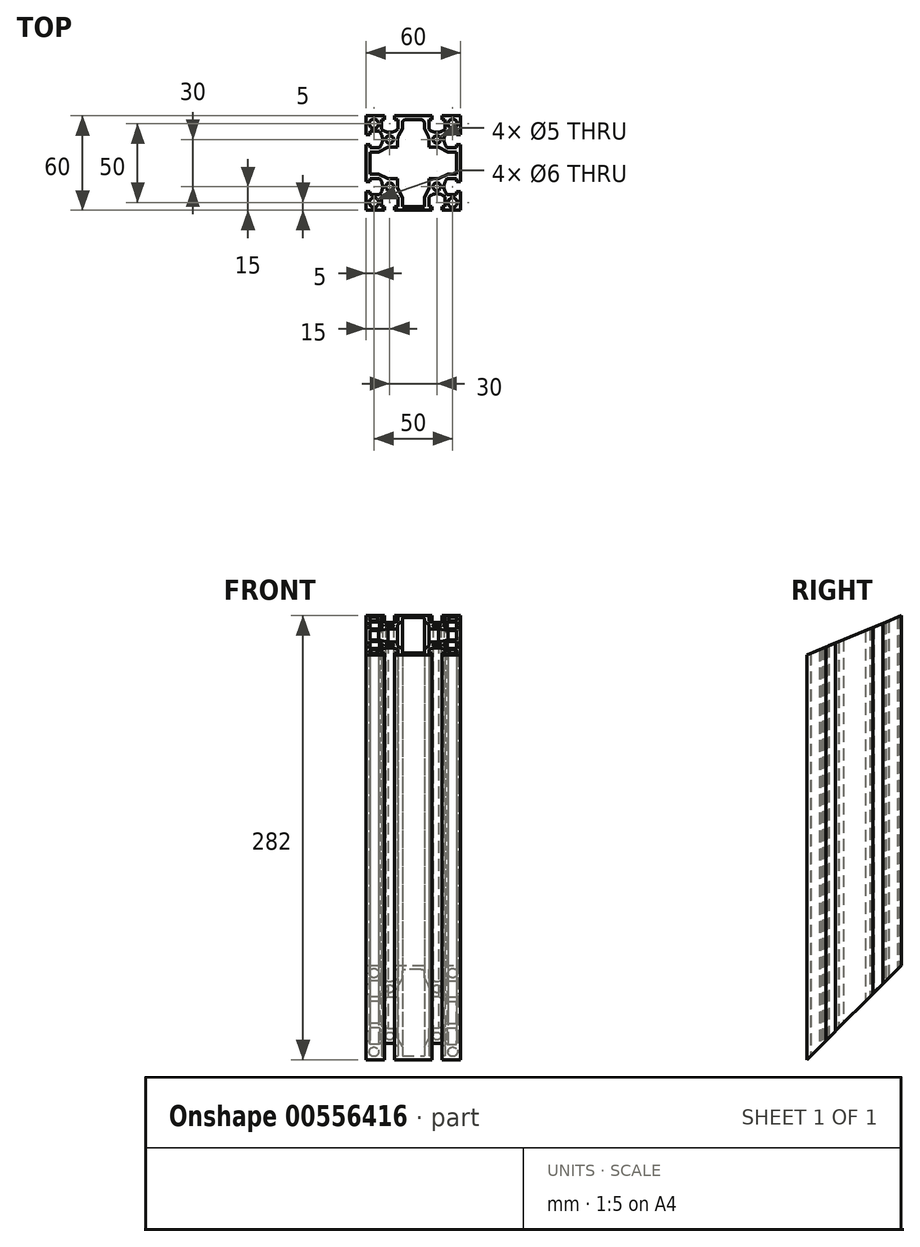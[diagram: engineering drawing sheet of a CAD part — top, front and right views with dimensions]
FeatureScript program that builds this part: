
annotation { "Feature Type Name" : "Feature", "Feature Type Description" : "" }
export const myFeature = defineFeature(function(context is Context, id is Id, definition is map)
    precondition{}
    {
        {
            var Q0;
            Q0=qCreatedBy(makeId("Top.planeOp"),FACE);
            var sketch = newSketch(context, id + "F0", { "sketchPlane" : qUnion([Q0])});
            skLineSegment(sketch, "E0.bottom", {"start": v(30, -30) * mm, "end": v(-30, -30) * mm});
            skLineSegment(sketch, "E0.top", {"start": v(30, 30) * mm, "end": v(-30, 30) * mm});
            skLineSegment(sketch, "E0.left", {"start": v(30, -30) * mm, "end": v(30, 30) * mm});
            skLineSegment(sketch, "E0.right", {"start": v(-30, -30) * mm, "end": v(-30, 30) * mm});
            skPoint(sketch, "E0.middle", {"position": v(0, 0) * mm});
            skLineSegment(sketch, "E1.top", {"start": v(-11.85, 30) * mm, "end": v(-18.15, 30) * mm});
            skLineSegment(sketch, "E1.left", {"start": v(-11.85, 27.5) * mm, "end": v(-11.85, 30) * mm});
            skLineSegment(sketch, "E1.right", {"start": v(-18.15, 27.5) * mm, "end": v(-18.15, 30) * mm});
            skPoint(sketch, "E1.middle", {"position": v(-15, 28.75) * mm});
            skLineSegment(sketch, "E2.bottom", {"start": v(-9.85, 27.5) * mm, "end": v(-11.85, 27.5) * mm});
            skLineSegment(sketch, "E2.left", {"start": v(-9.85, 27.5) * mm, "end": v(-9.85, 21.55) * mm});
            skLineSegment(sketch, "E2.right", {"start": v(-20.15, 27.5) * mm, "end": v(-20.15, 21.55) * mm});
            skPoint(sketch, "E2.middle", {"position": v(-15, 24.52) * mm});
            skArc(sketch, "E3", {"start": v(-20.15, 21.55) * mm, "mid": v(-15, 19.5) * mm, "end": v(-9.85, 21.55) * mm});
            skPoint(sketch, "E4.MirrorP", {"position": v(15, 24.52) * mm});
            skPoint(sketch, "E5.MirrorP", {"position": v(15, 28.75) * mm});
            skLineSegment(sketch, "E6.MirrorCS", {"start": v(11.85, 27.5) * mm, "end": v(11.85, 30) * mm});
            skLineSegment(sketch, "E7.MirrorCS", {"start": v(18.15, 27.5) * mm, "end": v(18.15, 30) * mm});
            skLineSegment(sketch, "E8.MirrorCS", {"start": v(9.85, 27.5) * mm, "end": v(11.85, 27.5) * mm});
            skLineSegment(sketch, "E9.MirrorCS", {"start": v(9.85, 27.5) * mm, "end": v(9.85, 21.55) * mm});
            skArc(sketch, "E10.MirrorCS", {"start": v(20.15, 21.55) * mm, "mid": v(15, 19.5) * mm, "end": v(9.85, 21.55) * mm});
            skLineSegment(sketch, "E11.MirrorCS", {"start": v(20.15, 27.5) * mm, "end": v(20.15, 21.55) * mm});
            skLineSegment(sketch, "E12.MirrorCS", {"start": v(11.85, 30) * mm, "end": v(18.15, 30) * mm});
            skLineSegment(sketch, "E13.1.0", {"start": v(27.5, 20.15) * mm, "end": v(21.55, 20.15) * mm});
            skLineSegment(sketch, "E13.1.1", {"start": v(27.5, 9.85) * mm, "end": v(21.55, 9.85) * mm});
            skArc(sketch, "E13.1.2", {"start": v(21.55, 20.15) * mm, "mid": v(19.5, 15) * mm, "end": v(21.55, 9.85) * mm});
            skLineSegment(sketch, "E13.1.3", {"start": v(27.5, -9.85) * mm, "end": v(21.55, -9.85) * mm});
            skLineSegment(sketch, "E13.1.4", {"start": v(27.5, -20.15) * mm, "end": v(21.55, -20.15) * mm});
            skPoint(sketch, "E13.1.5", {"position": v(28.75, 15) * mm});
            skPoint(sketch, "E13.1.6", {"position": v(28.75, -15) * mm});
            skArc(sketch, "E13.1.7", {"start": v(21.55, -20.15) * mm, "mid": v(19.5, -15) * mm, "end": v(21.55, -9.85) * mm});
            skPoint(sketch, "E13.1.8", {"position": v(24.52, -15) * mm});
            skPoint(sketch, "E13.1.9", {"position": v(24.52, 15) * mm});
            skLineSegment(sketch, "E13.1.10", {"start": v(27.5, 9.85) * mm, "end": v(27.5, 20.15) * mm});
            skLineSegment(sketch, "E13.1.11", {"start": v(27.5, -11.85) * mm, "end": v(27.5, -18.15) * mm});
            skLineSegment(sketch, "E13.1.12", {"start": v(30, 11.85) * mm, "end": v(30, 18.15) * mm});
            skLineSegment(sketch, "E13.1.13", {"start": v(30, -11.85) * mm, "end": v(30, -18.15) * mm});
            skLineSegment(sketch, "E13.1.14", {"start": v(27.5, 18.15) * mm, "end": v(30, 18.15) * mm});
            skLineSegment(sketch, "E13.1.15", {"start": v(27.5, 11.85) * mm, "end": v(30, 11.85) * mm});
            skLineSegment(sketch, "E13.1.16", {"start": v(27.5, 11.85) * mm, "end": v(27.5, 18.15) * mm});
            skLineSegment(sketch, "E13.1.17", {"start": v(27.5, -9.85) * mm, "end": v(27.5, -20.15) * mm});
            skLineSegment(sketch, "E13.1.18", {"start": v(27.5, -18.15) * mm, "end": v(30, -18.15) * mm});
            skLineSegment(sketch, "E13.1.19", {"start": v(27.5, -11.85) * mm, "end": v(30, -11.85) * mm});
            skLineSegment(sketch, "E13.2.0", {"start": v(20.15, -27.5) * mm, "end": v(20.15, -21.55) * mm});
            skLineSegment(sketch, "E13.2.1", {"start": v(9.85, -27.5) * mm, "end": v(9.85, -21.55) * mm});
            skArc(sketch, "E13.2.2", {"start": v(20.15, -21.55) * mm, "mid": v(15, -19.5) * mm, "end": v(9.85, -21.55) * mm});
            skLineSegment(sketch, "E13.2.3", {"start": v(-9.85, -27.5) * mm, "end": v(-9.85, -21.55) * mm});
            skLineSegment(sketch, "E13.2.4", {"start": v(-20.15, -27.5) * mm, "end": v(-20.15, -21.55) * mm});
            skPoint(sketch, "E13.2.5", {"position": v(15, -28.75) * mm});
            skPoint(sketch, "E13.2.6", {"position": v(-15, -28.75) * mm});
            skArc(sketch, "E13.2.7", {"start": v(-20.15, -21.55) * mm, "mid": v(-15, -19.5) * mm, "end": v(-9.85, -21.55) * mm});
            skPoint(sketch, "E13.2.8", {"position": v(-15, -24.52) * mm});
            skPoint(sketch, "E13.2.9", {"position": v(15, -24.52) * mm});
            skLineSegment(sketch, "E13.2.10", {"start": v(9.85, -27.5) * mm, "end": v(20.15, -27.5) * mm});
            skLineSegment(sketch, "E13.2.11", {"start": v(-11.85, -27.5) * mm, "end": v(-18.15, -27.5) * mm});
            skLineSegment(sketch, "E13.2.12", {"start": v(11.85, -30) * mm, "end": v(18.15, -30) * mm});
            skLineSegment(sketch, "E13.2.13", {"start": v(-11.85, -30) * mm, "end": v(-18.15, -30) * mm});
            skLineSegment(sketch, "E13.2.14", {"start": v(18.15, -27.5) * mm, "end": v(18.15, -30) * mm});
            skLineSegment(sketch, "E13.2.15", {"start": v(11.85, -27.5) * mm, "end": v(11.85, -30) * mm});
            skLineSegment(sketch, "E13.2.16", {"start": v(11.85, -27.5) * mm, "end": v(18.15, -27.5) * mm});
            skLineSegment(sketch, "E13.2.17", {"start": v(-9.85, -27.5) * mm, "end": v(-20.15, -27.5) * mm});
            skLineSegment(sketch, "E13.2.18", {"start": v(-18.15, -27.5) * mm, "end": v(-18.15, -30) * mm});
            skLineSegment(sketch, "E13.2.19", {"start": v(-11.85, -27.5) * mm, "end": v(-11.85, -30) * mm});
            skLineSegment(sketch, "E13.3.0", {"start": v(-27.5, -20.15) * mm, "end": v(-21.55, -20.15) * mm});
            skLineSegment(sketch, "E13.3.1", {"start": v(-27.5, -9.85) * mm, "end": v(-21.55, -9.85) * mm});
            skArc(sketch, "E13.3.2", {"start": v(-21.55, -20.15) * mm, "mid": v(-19.5, -15) * mm, "end": v(-21.55, -9.85) * mm});
            skLineSegment(sketch, "E13.3.3", {"start": v(-27.5, 9.85) * mm, "end": v(-21.55, 9.85) * mm});
            skLineSegment(sketch, "E13.3.4", {"start": v(-27.5, 20.15) * mm, "end": v(-21.55, 20.15) * mm});
            skPoint(sketch, "E13.3.5", {"position": v(-28.75, -15) * mm});
            skPoint(sketch, "E13.3.6", {"position": v(-28.75, 15) * mm});
            skArc(sketch, "E13.3.7", {"start": v(-21.55, 20.15) * mm, "mid": v(-19.5, 15) * mm, "end": v(-21.55, 9.85) * mm});
            skPoint(sketch, "E13.3.8", {"position": v(-24.52, 15) * mm});
            skPoint(sketch, "E13.3.9", {"position": v(-24.52, -15) * mm});
            skLineSegment(sketch, "E13.3.10", {"start": v(-27.5, -9.85) * mm, "end": v(-27.5, -20.15) * mm});
            skLineSegment(sketch, "E13.3.11", {"start": v(-27.5, 11.85) * mm, "end": v(-27.5, 18.15) * mm});
            skLineSegment(sketch, "E13.3.12", {"start": v(-30, -11.85) * mm, "end": v(-30, -18.15) * mm});
            skLineSegment(sketch, "E13.3.13", {"start": v(-30, 11.85) * mm, "end": v(-30, 18.15) * mm});
            skLineSegment(sketch, "E13.3.14", {"start": v(-27.5, -18.15) * mm, "end": v(-30, -18.15) * mm});
            skLineSegment(sketch, "E13.3.15", {"start": v(-27.5, -11.85) * mm, "end": v(-30, -11.85) * mm});
            skLineSegment(sketch, "E13.3.16", {"start": v(-27.5, -11.85) * mm, "end": v(-27.5, -18.15) * mm});
            skLineSegment(sketch, "E13.3.17", {"start": v(-27.5, 9.85) * mm, "end": v(-27.5, 20.15) * mm});
            skLineSegment(sketch, "E13.3.18", {"start": v(-27.5, 18.15) * mm, "end": v(-30, 18.15) * mm});
            skLineSegment(sketch, "E13.3.19", {"start": v(-27.5, 11.85) * mm, "end": v(-30, 11.85) * mm});
            skLineSegment(sketch, "E13.anchor1", {"start": v(0, 0) * mm, "end": v(-20.15, 21.55) * mm, "construction": true});
            skLineSegment(sketch, "E13.anchor2", {"start": v(0, 0) * mm, "end": v(-21.55, -20.15) * mm, "construction": true});
            skLineSegment(sketch, "E14.trimOffspring", {"start": v(-18.15, 27.5) * mm, "end": v(-20.15, 27.5) * mm});
            skLineSegment(sketch, "E15.trimOffspring", {"start": v(18.15, 27.5) * mm, "end": v(20.15, 27.5) * mm});
            skCircle(sketch, "E16", {"center": v(-15, 15) * mm, "radius": 2.5 * mm});
            skCircle(sketch, "E17", {"center": v(-25, 25) * mm, "radius": 3 * mm});
            skCircle(sketch, "E18.MirrorC", {"center": v(25, 25) * mm, "radius": 3 * mm});
            skCircle(sketch, "E19.MirrorC", {"center": v(25, -25) * mm, "radius": 3 * mm});
            skCircle(sketch, "E20.MirrorC", {"center": v(-25, -25) * mm, "radius": 3 * mm});
            skCircle(sketch, "E21.MirrorC", {"center": v(15, 15) * mm, "radius": 2.5 * mm});
            skCircle(sketch, "E22.MirrorC", {"center": v(15, -15) * mm, "radius": 2.5 * mm});
            skCircle(sketch, "E23.MirrorC", {"center": v(-15, -15) * mm, "radius": 2.5 * mm});
            skLineSegment(sketch, "E24", {"start": v(-7, 27.5) * mm, "end": v(0, 27.5) * mm});
            skLineSegment(sketch, "E25", {"start": v(-7, 27.5) * mm, "end": v(-7, 22) * mm});
            skLineSegment(sketch, "E26", {"start": v(-10, 10) * mm, "end": v(-10, 16) * mm});
            skLineSegment(sketch, "E27", {"start": v(-10, 16) * mm, "end": v(-7, 22) * mm});
            skLineSegment(sketch, "E28.MirrorCS", {"start": v(10, 10) * mm, "end": v(10, 16) * mm});
            skLineSegment(sketch, "E29.MirrorCS", {"start": v(10, 16) * mm, "end": v(7, 22) * mm});
            skLineSegment(sketch, "E30.MirrorCS", {"start": v(7, 27.5) * mm, "end": v(0, 27.5) * mm});
            skLineSegment(sketch, "E31.MirrorCS", {"start": v(7, 27.5) * mm, "end": v(7, 22) * mm});
            skLineSegment(sketch, "E32.1.0", {"start": v(-10, -10) * mm, "end": v(-16, -10) * mm});
            skLineSegment(sketch, "E32.1.1", {"start": v(-16, -10) * mm, "end": v(-22, -7) * mm});
            skLineSegment(sketch, "E32.1.2", {"start": v(-27.5, -7) * mm, "end": v(-22, -7) * mm});
            skLineSegment(sketch, "E32.1.3", {"start": v(-27.5, -7) * mm, "end": v(-27.5, 0) * mm});
            skLineSegment(sketch, "E32.1.4", {"start": v(-27.5, 7) * mm, "end": v(-27.5, 0) * mm});
            skLineSegment(sketch, "E32.1.5", {"start": v(-27.5, 7) * mm, "end": v(-22, 7) * mm});
            skLineSegment(sketch, "E32.1.6", {"start": v(-16, 10) * mm, "end": v(-22, 7) * mm});
            skLineSegment(sketch, "E32.1.7", {"start": v(-10, 10) * mm, "end": v(-16, 10) * mm});
            skLineSegment(sketch, "E32.2.0", {"start": v(10, -10) * mm, "end": v(10, -16) * mm});
            skLineSegment(sketch, "E32.2.1", {"start": v(10, -16) * mm, "end": v(7, -22) * mm});
            skLineSegment(sketch, "E32.2.2", {"start": v(7, -27.5) * mm, "end": v(7, -22) * mm});
            skLineSegment(sketch, "E32.2.3", {"start": v(7, -27.5) * mm, "end": v(0, -27.5) * mm});
            skLineSegment(sketch, "E32.2.4", {"start": v(-7, -27.5) * mm, "end": v(0, -27.5) * mm});
            skLineSegment(sketch, "E32.2.5", {"start": v(-7, -27.5) * mm, "end": v(-7, -22) * mm});
            skLineSegment(sketch, "E32.2.6", {"start": v(-10, -16) * mm, "end": v(-7, -22) * mm});
            skLineSegment(sketch, "E32.2.7", {"start": v(-10, -10) * mm, "end": v(-10, -16) * mm});
            skLineSegment(sketch, "E32.3.0", {"start": v(10, 10) * mm, "end": v(16, 10) * mm});
            skLineSegment(sketch, "E32.3.1", {"start": v(16, 10) * mm, "end": v(22, 7) * mm});
            skLineSegment(sketch, "E32.3.2", {"start": v(27.5, 7) * mm, "end": v(22, 7) * mm});
            skLineSegment(sketch, "E32.3.3", {"start": v(27.5, 7) * mm, "end": v(27.5, 0) * mm});
            skLineSegment(sketch, "E32.3.4", {"start": v(27.5, -7) * mm, "end": v(27.5, 0) * mm});
            skLineSegment(sketch, "E32.3.5", {"start": v(27.5, -7) * mm, "end": v(22, -7) * mm});
            skLineSegment(sketch, "E32.3.6", {"start": v(16, -10) * mm, "end": v(22, -7) * mm});
            skLineSegment(sketch, "E32.3.7", {"start": v(10, -10) * mm, "end": v(16, -10) * mm});
            skSolve(sketch);
        }
        {
            var Q0;
            {var subQ30=sQuery(id+"F0.wireOp",EDGE,"E1.left");Q0=makeQuery(id+"F0.imprint","IMPRINT",FACE,{"disambiguationData":[TD([[makeQuery(id+"F0.imprint","IMPRINT",EDGE,{"derivedFrom":subQ30}),-1.0]])]});}
            extrude(context, id + "F1", {"entities" : qUnion([Q0]), "depth" : 282 * mm, "offsetDistance" : 25 * mm});
        }
        {
            var Q0;
            Q0=makeQuery(id+"F1.opExtrude","SWEPT_EDGE",EDGE,{"disambiguationData":[OSD([sQuery(id+"F0.wireOp",EDGE,"E24"),sQuery(id+"F0.wireOp",EDGE,"E25")])]});
            var Q1;
            Q1=makeQuery(id+"F1.opExtrude","SWEPT_EDGE",EDGE,{"disambiguationData":[OSD([sQuery(id+"F0.wireOp",EDGE,"E30.MirrorCS"),sQuery(id+"F0.wireOp",EDGE,"E31.MirrorCS")])]});
            var Q2;
            Q2=makeQuery(id+"F1.opExtrude","SWEPT_EDGE",EDGE,{"disambiguationData":[OSD([sQuery(id+"F0.wireOp",EDGE,"840db5bc-c403-45cd-90c7-254e62d9e8c5.3.2"),sQuery(id+"F0.wireOp",EDGE,"840db5bc-c403-45cd-90c7-254e62d9e8c5.3.3")])]});
            var Q3;
            Q3=makeQuery(id+"F1.opExtrude","SWEPT_EDGE",EDGE,{"disambiguationData":[OSD([sQuery(id+"F0.wireOp",EDGE,"840db5bc-c403-45cd-90c7-254e62d9e8c5.3.4"),sQuery(id+"F0.wireOp",EDGE,"840db5bc-c403-45cd-90c7-254e62d9e8c5.3.5")])]});
            var Q4;
            Q4=makeQuery(id+"F1.opExtrude","SWEPT_EDGE",EDGE,{"disambiguationData":[OSD([sQuery(id+"F0.wireOp",EDGE,"840db5bc-c403-45cd-90c7-254e62d9e8c5.1.4"),sQuery(id+"F0.wireOp",EDGE,"840db5bc-c403-45cd-90c7-254e62d9e8c5.1.5")])]});
            var Q5;
            Q5=makeQuery(id+"F1.opExtrude","SWEPT_EDGE",EDGE,{"disambiguationData":[OSD([sQuery(id+"F0.wireOp",EDGE,"840db5bc-c403-45cd-90c7-254e62d9e8c5.1.2"),sQuery(id+"F0.wireOp",EDGE,"840db5bc-c403-45cd-90c7-254e62d9e8c5.1.3")])]});
            var Q6;
            Q6=makeQuery(id+"F1.opExtrude","SWEPT_EDGE",EDGE,{"disambiguationData":[OSD([sQuery(id+"F0.wireOp",EDGE,"840db5bc-c403-45cd-90c7-254e62d9e8c5.2.2"),sQuery(id+"F0.wireOp",EDGE,"840db5bc-c403-45cd-90c7-254e62d9e8c5.2.3")])]});
            var Q7;
            Q7=makeQuery(id+"F1.opExtrude","SWEPT_EDGE",EDGE,{"disambiguationData":[OSD([sQuery(id+"F0.wireOp",EDGE,"840db5bc-c403-45cd-90c7-254e62d9e8c5.2.4"),sQuery(id+"F0.wireOp",EDGE,"840db5bc-c403-45cd-90c7-254e62d9e8c5.2.5")])]});
            fillet(context, id + "F2", {"entities" : qUnion([Q0, Q1, Q2, Q3, Q4, Q5, Q6, Q7]), "radius" : 2 * mm, "tangentPropagation" : true, "allowEdgeOverflow" : false});
        }
        {
            var Q0;
            Q0=makeQuery(id+"F1.opExtrude","SWEPT_EDGE",EDGE,{"disambiguationData":[OSD([sQuery(id+"F0.wireOp",EDGE,"E26"),sQuery(id+"F0.wireOp",EDGE,"E27")])]});
            var Q1;
            Q1=makeQuery(id+"F1.opExtrude","SWEPT_EDGE",EDGE,{"disambiguationData":[OSD([sQuery(id+"F0.wireOp",EDGE,"E28.MirrorCS"),sQuery(id+"F0.wireOp",EDGE,"E29.MirrorCS")])]});
            var Q2;
            Q2=makeQuery(id+"F1.opExtrude","SWEPT_EDGE",EDGE,{"disambiguationData":[OSD([sQuery(id+"F0.wireOp",EDGE,"840db5bc-c403-45cd-90c7-254e62d9e8c5.3.0"),sQuery(id+"F0.wireOp",EDGE,"840db5bc-c403-45cd-90c7-254e62d9e8c5.3.1")])]});
            var Q3;
            Q3=makeQuery(id+"F1.opExtrude","SWEPT_EDGE",EDGE,{"disambiguationData":[OSD([sQuery(id+"F0.wireOp",EDGE,"840db5bc-c403-45cd-90c7-254e62d9e8c5.1.6"),sQuery(id+"F0.wireOp",EDGE,"840db5bc-c403-45cd-90c7-254e62d9e8c5.1.7")])]});
            var Q4;
            Q4=makeQuery(id+"F1.opExtrude","SWEPT_EDGE",EDGE,{"disambiguationData":[OSD([sQuery(id+"F0.wireOp",EDGE,"840db5bc-c403-45cd-90c7-254e62d9e8c5.1.0"),sQuery(id+"F0.wireOp",EDGE,"840db5bc-c403-45cd-90c7-254e62d9e8c5.1.1")])]});
            var Q5;
            Q5=makeQuery(id+"F1.opExtrude","SWEPT_EDGE",EDGE,{"disambiguationData":[OSD([sQuery(id+"F0.wireOp",EDGE,"840db5bc-c403-45cd-90c7-254e62d9e8c5.3.6"),sQuery(id+"F0.wireOp",EDGE,"840db5bc-c403-45cd-90c7-254e62d9e8c5.3.7")])]});
            var Q6;
            Q6=makeQuery(id+"F1.opExtrude","SWEPT_EDGE",EDGE,{"disambiguationData":[OSD([sQuery(id+"F0.wireOp",EDGE,"840db5bc-c403-45cd-90c7-254e62d9e8c5.2.0"),sQuery(id+"F0.wireOp",EDGE,"840db5bc-c403-45cd-90c7-254e62d9e8c5.2.1")])]});
            var Q7;
            Q7=makeQuery(id+"F1.opExtrude","SWEPT_EDGE",EDGE,{"disambiguationData":[OSD([sQuery(id+"F0.wireOp",EDGE,"840db5bc-c403-45cd-90c7-254e62d9e8c5.2.6"),sQuery(id+"F0.wireOp",EDGE,"840db5bc-c403-45cd-90c7-254e62d9e8c5.2.7")])]});
            fillet(context, id + "F3", {"entities" : qUnion([Q0, Q1, Q2, Q3, Q4, Q5, Q6, Q7]), "radius" : 7 * mm, "tangentPropagation" : true, "allowEdgeOverflow" : false});
        }
        {
            var Q0;
            {var subQ0=sQuery(id+"F0.wireOp",EDGE,"E0.bottom");Q0=makeQuery(id+"F1.opExtrude","SWEPT_FACE",FACE,{"disambiguationData":[OSD([subQ0]),TDD([makeQuery(id+"F0.imprint","IMPRINT",EDGE,{"disambiguationData":[TD([[makeQuery(id+"F0.imprint","INTERSECT",VERTEX,{"derivedFrom":[subQ0,sQuery(id+"F0.wireOp",EDGE,"E13.2.12"),sQuery(id+"F0.wireOp",EDGE,"E13.2.15")]}),-1.0]])],"derivedFrom":subQ0})])]});}
            var sketch = newSketch(context, id + "F4", { "sketchPlane" : qUnion([Q0])});
            skLineSegment(sketch, "E33.0", {"start": v(-18.15, 282) * mm, "end": v(-30, 282) * mm});
            skLineSegment(sketch, "E33.1", {"start": v(30, 282) * mm, "end": v(30, 0) * mm});
            skLineSegment(sketch, "E34", {"start": v(-30, 282) * mm, "end": v(30, 282) * mm});
            skLineSegment(sketch, "E35", {"start": v(30, 222) * mm, "end": v(-30, 282) * mm});
            skLineSegment(sketch, "E36.0", {"start": v(-18.15, 0) * mm, "end": v(-30, 0) * mm});
            skLineSegment(sketch, "E37", {"start": v(-30, 0) * mm, "end": v(30, 0) * mm});
            skLineSegment(sketch, "E38", {"start": v(30, 60) * mm, "end": v(-30, 0) * mm});
            skSolve(sketch);
        }
        {
            var Q0;
            Q0=qCreatedBy(makeId("Right.planeOp"),FACE);
            var sketch = newSketch(context, id + "F5", { "sketchPlane" : qUnion([Q0])});
            skLineSegment(sketch, "E39.bottom", {"start": v(64.9, 94.9) * mm, "end": v(-30, 0) * mm});
            skLineSegment(sketch, "E39.top", {"start": v(115.26, 44.52) * mm, "end": v(20.37, -50.37) * mm});
            skLineSegment(sketch, "E39.left", {"start": v(64.9, 94.9) * mm, "end": v(115.26, 44.52) * mm});
            skLineSegment(sketch, "E39.right", {"start": v(-30, 0) * mm, "end": v(20.37, -50.37) * mm});
            skLineSegment(sketch, "E40.bottom", {"start": v(-7.72, 373.07) * mm, "end": v(-157.96, 310.84) * mm});
            skLineSegment(sketch, "E40.top", {"start": v(30, 282) * mm, "end": v(-120.24, 219.77) * mm});
            skLineSegment(sketch, "E40.left", {"start": v(-7.72, 373.07) * mm, "end": v(30, 282) * mm});
            skLineSegment(sketch, "E40.right", {"start": v(-157.96, 310.84) * mm, "end": v(-120.24, 219.77) * mm});
            skSolve(sketch);
        }
        {
            var Q0;
            Q0=qSketchRegion(id+"F5",true);
            extrude(context, id + "F6", {"entities" : qUnion([Q0]), "operationType" : NewBodyOperationType.REMOVE, "depth" : 30 * mm, "offsetDistance" : 25 * mm, "hasSecondDirection" : true, "secondDirectionOppositeDirection" : true, "secondDirectionDepth" : 30 * mm});
        }
    });
